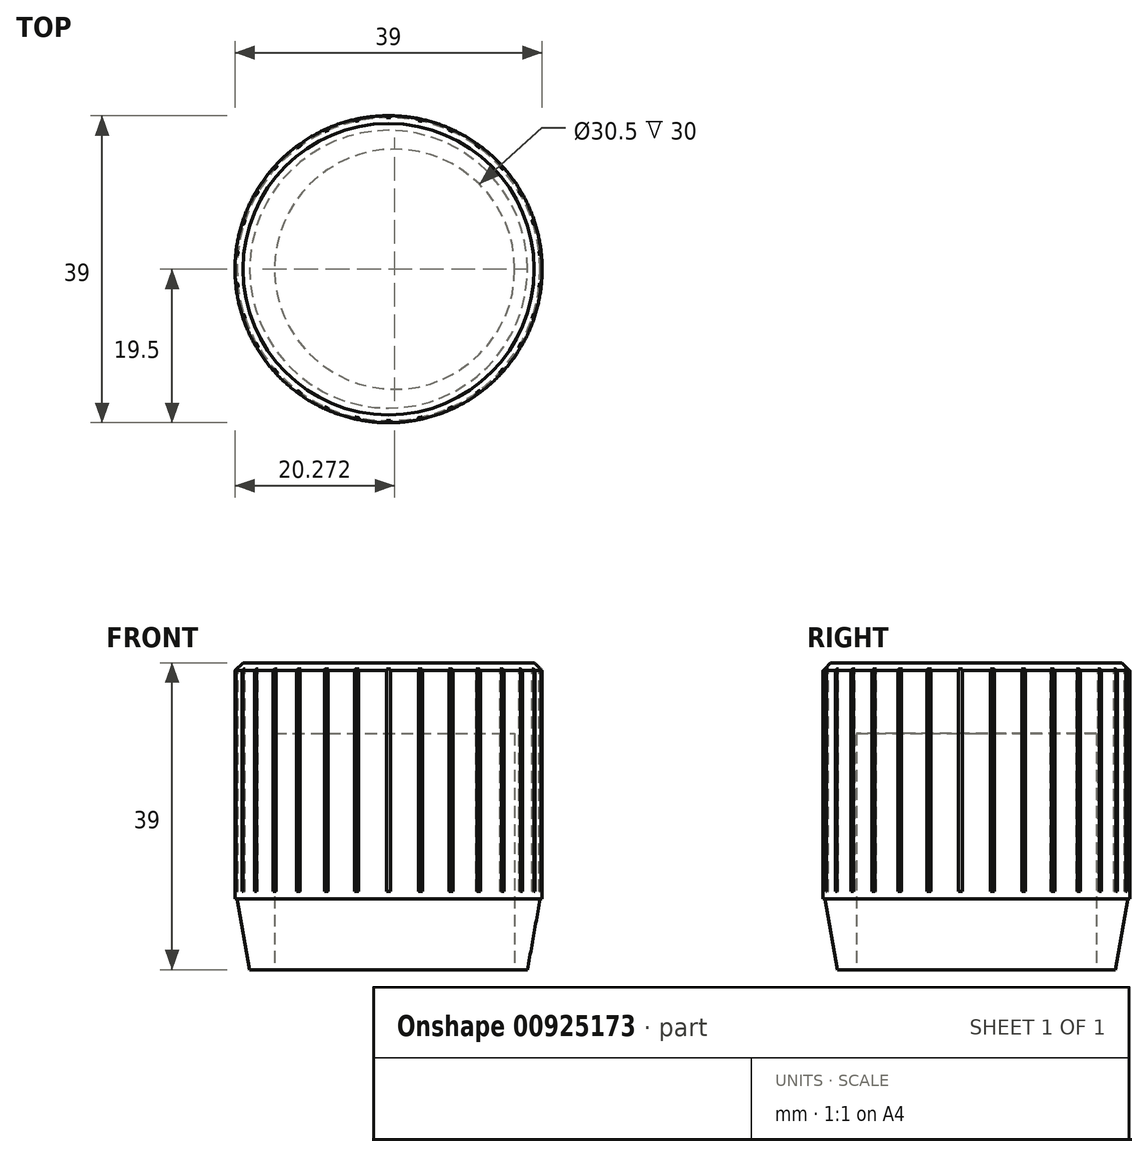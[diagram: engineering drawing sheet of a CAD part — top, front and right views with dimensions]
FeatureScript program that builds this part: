
annotation { "Feature Type Name" : "Feature", "Feature Type Description" : "" }
export const myFeature = defineFeature(function(context is Context, id is Id, definition is map)
    precondition{}
    {
        {
            var Q0;
            Q0=qCreatedBy(makeId("Top.planeOp"),FACE);
            var sketch = newSketch(context, id + "F0", { "sketchPlane" : qUnion([Q0])});
            skCircle(sketch, "E0", {"center": v(0, 0) * mm, "radius": 19.5 * mm});
            skSolve(sketch);
        }
        {
            var Q0;
            Q0=makeQuery(id+"F0.imprint","IMPRINT",FACE,{"disambiguationData":[TD([[makeQuery(id+"F0.imprint","IMPRINT",EDGE,{"derivedFrom":sQuery(id+"F0.wireOp",EDGE,"E0")}),1.0]])]});
            extrude(context, id + "F1", {"entities" : qUnion([Q0]), "oppositeDirection" : true, "depth" : 30 * mm, "offsetDistance" : 25 * mm});
        }
        {
            var Q0;
            Q0=makeQuery(id+"F1.opExtrude","CAP_EDGE",EDGE,{"disambiguationData":[OSD([sQuery(id+"F0.wireOp",EDGE,"E0")])],"isStart":true});
            chamfer(context, id + "F2", {"entities" : qUnion([Q0]), "width" : 1 * mm, "tangentPropagation" : true});
        }
        {
            var Q0;
            Q0=qCreatedBy(makeId("Front.planeOp"),FACE);
            var sketch = newSketch(context, id + "F3", { "sketchPlane" : qUnion([Q0])});
            skLineSegment(sketch, "E1", {"start": v(0, 0) * mm, "end": v(0, -30) * mm});
            skLineSegment(sketch, "E2", {"start": v(0, -30) * mm, "end": v(19.25, -30) * mm});
            skLineSegment(sketch, "E3", {"start": v(0, -30) * mm, "end": v(0, -39) * mm});
            skLineSegment(sketch, "E4", {"start": v(0, -39) * mm, "end": v(17.64, -39) * mm});
            skLineSegment(sketch, "E5", {"start": v(17.64, -39) * mm, "end": v(19.25, -30) * mm});
            skSolve(sketch);
        }
        {
            var Q0;
            Q0=makeQuery(id+"F3.imprint","IMPRINT",FACE,{"disambiguationData":[TD([[makeQuery(id+"F3.imprint","IMPRINT",EDGE,{"derivedFrom":sQuery(id+"F3.wireOp",EDGE,"E2")}),-1.0]])]});
            var Q1;
            Q1=sQuery(id+"F3.wireOp",EDGE,"E3");
            revolve(context, id + "F4", {"operationType" : NewBodyOperationType.ADD, "surfaceOperationType" : NewSurfaceOperationType.NEW, "entities" : qUnion([Q0]), "axis" : qUnion([Q1]), "revolveType" : RevolveType.FULL});
        }
        {
            var Q0;
            Q0=makeQuery(id+"F4.opRevolve","SWEPT_FACE",FACE,{"disambiguationData":[OSD([sQuery(id+"F3.wireOp",EDGE,"E4")])]});
            var sketch = newSketch(context, id + "F5", { "sketchPlane" : qUnion([Q0])});
            skCircle(sketch, "E6", {"center": v(0.77, 0) * mm, "radius": 15.25 * mm});
            skSolve(sketch);
        }
        {
            var Q0;
            Q0=makeQuery(id+"F5.imprint","IMPRINT",FACE,{"disambiguationData":[TD([[makeQuery(id+"F5.imprint","IMPRINT",EDGE,{"derivedFrom":sQuery(id+"F5.wireOp",EDGE,"E6")}),1.0]])]});
            extrude(context, id + "F6", {"entities" : qUnion([Q0]), "operationType" : NewBodyOperationType.REMOVE, "oppositeDirection" : true, "depth" : 30 * mm, "offsetDistance" : 25 * mm});
        }
        {
            var Q0;
            Q0=makeQuery(id+"F1.opExtrude","CAP_FACE",FACE,{"disambiguationData":[OSD([sQuery(id+"F0.wireOp",EDGE,"E0")])],"isStart":true});
            var sketch = newSketch(context, id + "F7", { "sketchPlane" : qUnion([Q0])});
            skLineSegment(sketch, "E7", {"start": v(0, 0) * mm, "end": v(0, 18.5) * mm});
            skPoint(sketch, "E8", {"position": v(0, 19.5) * mm});
            skLineSegment(sketch, "E9.bottom", {"start": v(0.25, 19.25) * mm, "end": v(-0.25, 19.25) * mm});
            skLineSegment(sketch, "E9.top", {"start": v(0.25, 19.75) * mm, "end": v(-0.25, 19.75) * mm});
            skLineSegment(sketch, "E9.left", {"start": v(0.25, 19.25) * mm, "end": v(0.25, 19.75) * mm});
            skLineSegment(sketch, "E9.right", {"start": v(-0.25, 19.25) * mm, "end": v(-0.25, 19.75) * mm});
            skPoint(sketch, "E10.center", {"position": v(0, 0) * mm});
            skLineSegment(sketch, "E11.1.0", {"start": v(-4.25, 18.78) * mm, "end": v(-4.35, 19.27) * mm});
            skLineSegment(sketch, "E11.1.1", {"start": v(-3.76, 18.88) * mm, "end": v(-4.25, 18.78) * mm});
            skLineSegment(sketch, "E11.1.2", {"start": v(-3.86, 19.37) * mm, "end": v(-4.35, 19.27) * mm});
            skLineSegment(sketch, "E11.1.3", {"start": v(-3.76, 18.88) * mm, "end": v(-3.86, 19.37) * mm});
            skLineSegment(sketch, "E11.2.0", {"start": v(-8.06, 17.49) * mm, "end": v(-8.26, 17.94) * mm});
            skLineSegment(sketch, "E11.2.1", {"start": v(-7.6, 17.69) * mm, "end": v(-8.06, 17.49) * mm});
            skLineSegment(sketch, "E11.2.2", {"start": v(-7.8, 18.15) * mm, "end": v(-8.26, 17.94) * mm});
            skLineSegment(sketch, "E11.2.3", {"start": v(-7.6, 17.69) * mm, "end": v(-7.8, 18.15) * mm});
            skLineSegment(sketch, "E11.3.0", {"start": v(-11.52, 15.43) * mm, "end": v(-11.81, 15.83) * mm});
            skLineSegment(sketch, "E11.3.1", {"start": v(-11.11, 15.72) * mm, "end": v(-11.52, 15.43) * mm});
            skLineSegment(sketch, "E11.3.2", {"start": v(-11.4, 16.13) * mm, "end": v(-11.81, 15.83) * mm});
            skLineSegment(sketch, "E11.3.3", {"start": v(-11.11, 15.72) * mm, "end": v(-11.4, 16.13) * mm});
            skLineSegment(sketch, "E11.4.0", {"start": v(-14.47, 12.7) * mm, "end": v(-14.85, 13.03) * mm});
            skLineSegment(sketch, "E11.4.1", {"start": v(-14.14, 13.07) * mm, "end": v(-14.47, 12.7) * mm});
            skLineSegment(sketch, "E11.4.2", {"start": v(-14.51, 13.4) * mm, "end": v(-14.85, 13.03) * mm});
            skLineSegment(sketch, "E11.4.3", {"start": v(-14.14, 13.07) * mm, "end": v(-14.51, 13.4) * mm});
            skLineSegment(sketch, "E11.5.0", {"start": v(-16.8, 9.4) * mm, "end": v(-17.23, 9.66) * mm});
            skLineSegment(sketch, "E11.5.1", {"start": v(-16.55, 9.84) * mm, "end": v(-16.8, 9.4) * mm});
            skLineSegment(sketch, "E11.5.2", {"start": v(-16.98, 10.1) * mm, "end": v(-17.23, 9.66) * mm});
            skLineSegment(sketch, "E11.5.3", {"start": v(-16.55, 9.84) * mm, "end": v(-16.98, 10.1) * mm});
            skLineSegment(sketch, "E11.6.0", {"start": v(-18.39, 5.71) * mm, "end": v(-18.86, 5.87) * mm});
            skLineSegment(sketch, "E11.6.1", {"start": v(-18.23, 6.19) * mm, "end": v(-18.39, 5.71) * mm});
            skLineSegment(sketch, "E11.6.2", {"start": v(-18.7, 6.34) * mm, "end": v(-18.86, 5.87) * mm});
            skLineSegment(sketch, "E11.6.3", {"start": v(-18.23, 6.19) * mm, "end": v(-18.7, 6.34) * mm});
            skLineSegment(sketch, "E11.7.0", {"start": v(-19.17, 1.76) * mm, "end": v(-19.67, 1.82) * mm});
            skLineSegment(sketch, "E11.7.1", {"start": v(-19.12, 2.26) * mm, "end": v(-19.17, 1.76) * mm});
            skLineSegment(sketch, "E11.7.2", {"start": v(-19.62, 2.31) * mm, "end": v(-19.67, 1.82) * mm});
            skLineSegment(sketch, "E11.7.3", {"start": v(-19.12, 2.26) * mm, "end": v(-19.62, 2.31) * mm});
            skLineSegment(sketch, "E11.8.0", {"start": v(-19.12, -2.26) * mm, "end": v(-19.62, -2.31) * mm});
            skLineSegment(sketch, "E11.8.1", {"start": v(-19.17, -1.76) * mm, "end": v(-19.12, -2.26) * mm});
            skLineSegment(sketch, "E11.8.2", {"start": v(-19.67, -1.82) * mm, "end": v(-19.62, -2.31) * mm});
            skLineSegment(sketch, "E11.8.3", {"start": v(-19.17, -1.76) * mm, "end": v(-19.67, -1.82) * mm});
            skLineSegment(sketch, "E11.9.0", {"start": v(-18.23, -6.19) * mm, "end": v(-18.7, -6.34) * mm});
            skLineSegment(sketch, "E11.9.1", {"start": v(-18.39, -5.71) * mm, "end": v(-18.23, -6.19) * mm});
            skLineSegment(sketch, "E11.9.2", {"start": v(-18.86, -5.87) * mm, "end": v(-18.7, -6.34) * mm});
            skLineSegment(sketch, "E11.9.3", {"start": v(-18.39, -5.71) * mm, "end": v(-18.86, -5.87) * mm});
            skLineSegment(sketch, "E11.10.0", {"start": v(-16.55, -9.84) * mm, "end": v(-16.98, -10.1) * mm});
            skLineSegment(sketch, "E11.10.1", {"start": v(-16.8, -9.4) * mm, "end": v(-16.55, -9.84) * mm});
            skLineSegment(sketch, "E11.10.2", {"start": v(-17.23, -9.66) * mm, "end": v(-16.98, -10.1) * mm});
            skLineSegment(sketch, "E11.10.3", {"start": v(-16.8, -9.4) * mm, "end": v(-17.23, -9.66) * mm});
            skLineSegment(sketch, "E11.11.0", {"start": v(-14.14, -13.07) * mm, "end": v(-14.51, -13.4) * mm});
            skLineSegment(sketch, "E11.11.1", {"start": v(-14.47, -12.7) * mm, "end": v(-14.14, -13.07) * mm});
            skLineSegment(sketch, "E11.11.2", {"start": v(-14.85, -13.03) * mm, "end": v(-14.51, -13.4) * mm});
            skLineSegment(sketch, "E11.11.3", {"start": v(-14.47, -12.7) * mm, "end": v(-14.85, -13.03) * mm});
            skLineSegment(sketch, "E11.12.0", {"start": v(-11.11, -15.72) * mm, "end": v(-11.4, -16.13) * mm});
            skLineSegment(sketch, "E11.12.1", {"start": v(-11.52, -15.43) * mm, "end": v(-11.11, -15.72) * mm});
            skLineSegment(sketch, "E11.12.2", {"start": v(-11.81, -15.83) * mm, "end": v(-11.4, -16.13) * mm});
            skLineSegment(sketch, "E11.12.3", {"start": v(-11.52, -15.43) * mm, "end": v(-11.81, -15.83) * mm});
            skLineSegment(sketch, "E11.13.0", {"start": v(-7.6, -17.69) * mm, "end": v(-7.8, -18.15) * mm});
            skLineSegment(sketch, "E11.13.1", {"start": v(-8.06, -17.49) * mm, "end": v(-7.6, -17.69) * mm});
            skLineSegment(sketch, "E11.13.2", {"start": v(-8.26, -17.94) * mm, "end": v(-7.8, -18.15) * mm});
            skLineSegment(sketch, "E11.13.3", {"start": v(-8.06, -17.49) * mm, "end": v(-8.26, -17.94) * mm});
            skLineSegment(sketch, "E11.14.0", {"start": v(-3.76, -18.88) * mm, "end": v(-3.86, -19.37) * mm});
            skLineSegment(sketch, "E11.14.1", {"start": v(-4.25, -18.78) * mm, "end": v(-3.76, -18.88) * mm});
            skLineSegment(sketch, "E11.14.2", {"start": v(-4.35, -19.27) * mm, "end": v(-3.86, -19.37) * mm});
            skLineSegment(sketch, "E11.14.3", {"start": v(-4.25, -18.78) * mm, "end": v(-4.35, -19.27) * mm});
            skLineSegment(sketch, "E11.15.0", {"start": v(0.25, -19.25) * mm, "end": v(0.25, -19.75) * mm});
            skLineSegment(sketch, "E11.15.1", {"start": v(-0.25, -19.25) * mm, "end": v(0.25, -19.25) * mm});
            skLineSegment(sketch, "E11.15.2", {"start": v(-0.25, -19.75) * mm, "end": v(0.25, -19.75) * mm});
            skLineSegment(sketch, "E11.15.3", {"start": v(-0.25, -19.25) * mm, "end": v(-0.25, -19.75) * mm});
            skLineSegment(sketch, "E11.16.0", {"start": v(4.25, -18.78) * mm, "end": v(4.35, -19.27) * mm});
            skLineSegment(sketch, "E11.16.1", {"start": v(3.76, -18.88) * mm, "end": v(4.25, -18.78) * mm});
            skLineSegment(sketch, "E11.16.2", {"start": v(3.86, -19.37) * mm, "end": v(4.35, -19.27) * mm});
            skLineSegment(sketch, "E11.16.3", {"start": v(3.76, -18.88) * mm, "end": v(3.86, -19.37) * mm});
            skLineSegment(sketch, "E11.17.0", {"start": v(8.06, -17.49) * mm, "end": v(8.26, -17.94) * mm});
            skLineSegment(sketch, "E11.17.1", {"start": v(7.6, -17.69) * mm, "end": v(8.06, -17.49) * mm});
            skLineSegment(sketch, "E11.17.2", {"start": v(7.8, -18.15) * mm, "end": v(8.26, -17.94) * mm});
            skLineSegment(sketch, "E11.17.3", {"start": v(7.6, -17.69) * mm, "end": v(7.8, -18.15) * mm});
            skLineSegment(sketch, "E11.18.0", {"start": v(11.52, -15.43) * mm, "end": v(11.81, -15.83) * mm});
            skLineSegment(sketch, "E11.18.1", {"start": v(11.11, -15.72) * mm, "end": v(11.52, -15.43) * mm});
            skLineSegment(sketch, "E11.18.2", {"start": v(11.4, -16.13) * mm, "end": v(11.81, -15.83) * mm});
            skLineSegment(sketch, "E11.18.3", {"start": v(11.11, -15.72) * mm, "end": v(11.4, -16.13) * mm});
            skLineSegment(sketch, "E11.19.0", {"start": v(14.47, -12.7) * mm, "end": v(14.85, -13.03) * mm});
            skLineSegment(sketch, "E11.19.1", {"start": v(14.14, -13.07) * mm, "end": v(14.47, -12.7) * mm});
            skLineSegment(sketch, "E11.19.2", {"start": v(14.51, -13.4) * mm, "end": v(14.85, -13.03) * mm});
            skLineSegment(sketch, "E11.19.3", {"start": v(14.14, -13.07) * mm, "end": v(14.51, -13.4) * mm});
            skLineSegment(sketch, "E11.20.0", {"start": v(16.8, -9.4) * mm, "end": v(17.23, -9.66) * mm});
            skLineSegment(sketch, "E11.20.1", {"start": v(16.55, -9.84) * mm, "end": v(16.8, -9.4) * mm});
            skLineSegment(sketch, "E11.20.2", {"start": v(16.98, -10.1) * mm, "end": v(17.23, -9.66) * mm});
            skLineSegment(sketch, "E11.20.3", {"start": v(16.55, -9.84) * mm, "end": v(16.98, -10.1) * mm});
            skLineSegment(sketch, "E11.21.0", {"start": v(18.39, -5.71) * mm, "end": v(18.86, -5.87) * mm});
            skLineSegment(sketch, "E11.21.1", {"start": v(18.23, -6.19) * mm, "end": v(18.39, -5.71) * mm});
            skLineSegment(sketch, "E11.21.2", {"start": v(18.7, -6.34) * mm, "end": v(18.86, -5.87) * mm});
            skLineSegment(sketch, "E11.21.3", {"start": v(18.23, -6.19) * mm, "end": v(18.7, -6.34) * mm});
            skLineSegment(sketch, "E11.22.0", {"start": v(19.17, -1.76) * mm, "end": v(19.67, -1.82) * mm});
            skLineSegment(sketch, "E11.22.1", {"start": v(19.12, -2.26) * mm, "end": v(19.17, -1.76) * mm});
            skLineSegment(sketch, "E11.22.2", {"start": v(19.62, -2.31) * mm, "end": v(19.67, -1.82) * mm});
            skLineSegment(sketch, "E11.22.3", {"start": v(19.12, -2.26) * mm, "end": v(19.62, -2.31) * mm});
            skLineSegment(sketch, "E11.23.0", {"start": v(19.12, 2.26) * mm, "end": v(19.62, 2.31) * mm});
            skLineSegment(sketch, "E11.23.1", {"start": v(19.17, 1.76) * mm, "end": v(19.12, 2.26) * mm});
            skLineSegment(sketch, "E11.23.2", {"start": v(19.67, 1.82) * mm, "end": v(19.62, 2.31) * mm});
            skLineSegment(sketch, "E11.23.3", {"start": v(19.17, 1.76) * mm, "end": v(19.67, 1.82) * mm});
            skLineSegment(sketch, "E11.24.0", {"start": v(18.23, 6.19) * mm, "end": v(18.7, 6.34) * mm});
            skLineSegment(sketch, "E11.24.1", {"start": v(18.39, 5.71) * mm, "end": v(18.23, 6.19) * mm});
            skLineSegment(sketch, "E11.24.2", {"start": v(18.86, 5.87) * mm, "end": v(18.7, 6.34) * mm});
            skLineSegment(sketch, "E11.24.3", {"start": v(18.39, 5.71) * mm, "end": v(18.86, 5.87) * mm});
            skLineSegment(sketch, "E11.25.0", {"start": v(16.55, 9.84) * mm, "end": v(16.98, 10.1) * mm});
            skLineSegment(sketch, "E11.25.1", {"start": v(16.8, 9.4) * mm, "end": v(16.55, 9.84) * mm});
            skLineSegment(sketch, "E11.25.2", {"start": v(17.23, 9.66) * mm, "end": v(16.98, 10.1) * mm});
            skLineSegment(sketch, "E11.25.3", {"start": v(16.8, 9.4) * mm, "end": v(17.23, 9.66) * mm});
            skLineSegment(sketch, "E11.26.0", {"start": v(14.14, 13.07) * mm, "end": v(14.51, 13.4) * mm});
            skLineSegment(sketch, "E11.26.1", {"start": v(14.47, 12.7) * mm, "end": v(14.14, 13.07) * mm});
            skLineSegment(sketch, "E11.26.2", {"start": v(14.85, 13.03) * mm, "end": v(14.51, 13.4) * mm});
            skLineSegment(sketch, "E11.26.3", {"start": v(14.47, 12.7) * mm, "end": v(14.85, 13.03) * mm});
            skLineSegment(sketch, "E11.27.0", {"start": v(11.11, 15.72) * mm, "end": v(11.4, 16.13) * mm});
            skLineSegment(sketch, "E11.27.1", {"start": v(11.52, 15.43) * mm, "end": v(11.11, 15.72) * mm});
            skLineSegment(sketch, "E11.27.2", {"start": v(11.81, 15.83) * mm, "end": v(11.4, 16.13) * mm});
            skLineSegment(sketch, "E11.27.3", {"start": v(11.52, 15.43) * mm, "end": v(11.81, 15.83) * mm});
            skLineSegment(sketch, "E11.28.0", {"start": v(7.6, 17.69) * mm, "end": v(7.8, 18.15) * mm});
            skLineSegment(sketch, "E11.28.1", {"start": v(8.06, 17.49) * mm, "end": v(7.6, 17.69) * mm});
            skLineSegment(sketch, "E11.28.2", {"start": v(8.26, 17.94) * mm, "end": v(7.8, 18.15) * mm});
            skLineSegment(sketch, "E11.28.3", {"start": v(8.06, 17.49) * mm, "end": v(8.26, 17.94) * mm});
            skLineSegment(sketch, "E11.29.0", {"start": v(3.76, 18.88) * mm, "end": v(3.86, 19.37) * mm});
            skLineSegment(sketch, "E11.29.1", {"start": v(4.25, 18.78) * mm, "end": v(3.76, 18.88) * mm});
            skLineSegment(sketch, "E11.29.2", {"start": v(4.35, 19.27) * mm, "end": v(3.86, 19.37) * mm});
            skLineSegment(sketch, "E11.29.3", {"start": v(4.25, 18.78) * mm, "end": v(4.35, 19.27) * mm});
            skSolve(sketch);
        }
        {
            var Q0;
            Q0 = qSketchRegion(id + "F7", true);
            extrude(context, id + "F8", {"entities" : qUnion([Q0]), "operationType" : NewBodyOperationType.REMOVE, "oppositeDirection" : true, "depth" : 29.03 * mm, "offsetDistance" : 25 * mm});
        }
    });
